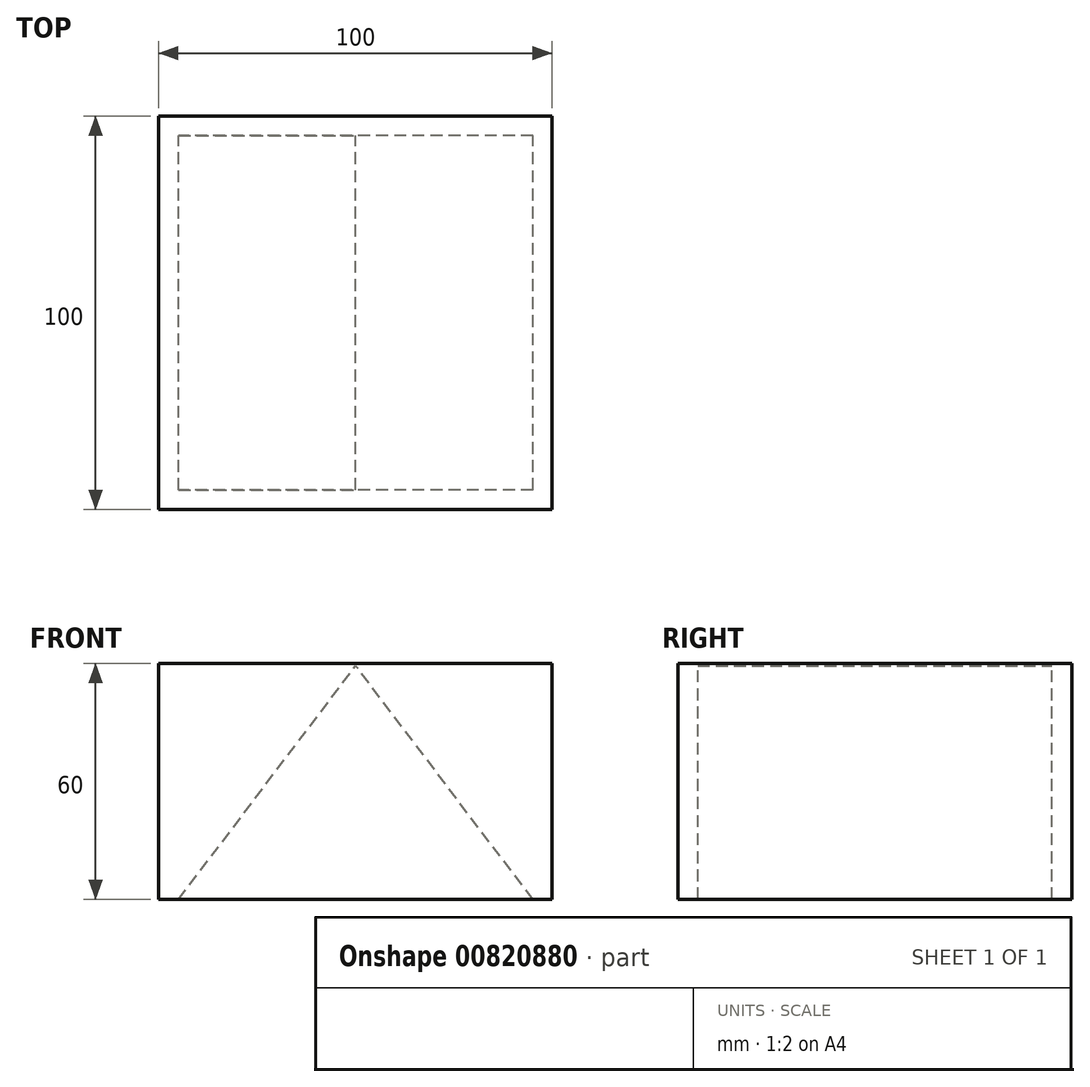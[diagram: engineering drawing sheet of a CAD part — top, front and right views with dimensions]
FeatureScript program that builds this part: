
annotation { "Feature Type Name" : "Feature", "Feature Type Description" : "" }
export const myFeature = defineFeature(function(context is Context, id is Id, definition is map)
    precondition{}
    {
        {
            var Q0;
            Q0=qCreatedBy(makeId("Top.planeOp"),FACE);
            var sketch = newSketch(context, id + "F0", { "sketchPlane" : qUnion([Q0])});
            skLineSegment(sketch, "E0.bottom", {"start": v(0, 0) * mm, "end": v(-100, 0) * mm});
            skLineSegment(sketch, "E0.top", {"start": v(0, 100) * mm, "end": v(-100, 100) * mm});
            skLineSegment(sketch, "E0.left", {"start": v(0, 0) * mm, "end": v(0, 100) * mm});
            skLineSegment(sketch, "E0.right", {"start": v(-100, 0) * mm, "end": v(-100, 100) * mm});
            skSolve(sketch);
        }
        {
            var Q0;
            Q0=makeQuery(id+"F0.imprint","IMPRINT",FACE,{"disambiguationData":[TD([[makeQuery(id+"F0.imprint","IMPRINT",EDGE,{"derivedFrom":sQuery(id+"F0.wireOp",EDGE,"E0.bottom")}),-1.0]])]});
            extrude(context, id + "F1", {"entities" : qUnion([Q0]), "depth" : 60 * mm, "offsetDistance" : 25.4 * mm});
        }
        {
            var Q0;
            Q0=makeQuery(id+"F1.opExtrude","SWEPT_FACE",FACE,{"disambiguationData":[OSD([sQuery(id+"F0.wireOp",EDGE,"E0.top")])]});
            cPlane(context, id + "F2", {"entities" : qUnion([Q0]), "cplaneType" : CPlaneType.OFFSET, "offset" : 5 * mm, "oppositeDirection" : true, "width" : 152.4 * mm, "height" : 152.4 * mm});
        }
        {
            var Q0;
            Q0=makeQuery(id+"F1.opExtrude","SWEPT_FACE",FACE,{"disambiguationData":[OSD([sQuery(id+"F0.wireOp",EDGE,"E0.left")])]});
            cPlane(context, id + "F3", {"entities" : qUnion([Q0]), "cplaneType" : CPlaneType.OFFSET, "offset" : 5 * mm, "oppositeDirection" : true, "width" : 152.4 * mm, "height" : 152.4 * mm});
        }
        {
            var Q0;
            Q0=qCreatedBy(id+"F2.planeOp",FACE);
            var sketch = newSketch(context, id + "F4", { "sketchPlane" : qUnion([Q0])});
            skLineSegment(sketch, "E1", {"start": v(4.9, 0) * mm, "end": v(49.9, 59.36) * mm});
            skLineSegment(sketch, "E2", {"start": v(4.9, 0) * mm, "end": v(4.9, 60) * mm, "construction": true});
            skLineSegment(sketch, "E3", {"start": v(4.9, 60) * mm, "end": v(49.9, 59.36) * mm, "construction": true});
            skLineSegment(sketch, "E4", {"start": v(49.9, 59.36) * mm, "end": v(49.9, 0) * mm, "construction": true});
            skLineSegment(sketch, "E5.MirrorCS", {"start": v(94.9, 0) * mm, "end": v(49.9, 59.36) * mm});
            skLineSegment(sketch, "E6", {"start": v(4.9, 0) * mm, "end": v(94.9, 0) * mm});
            skSolve(sketch);
        }
        {
            var Q0;
            Q0=qSketchRegion(id+"F4",true);
            extrude(context, id + "F5", {"entities" : qUnion([Q0]), "operationType" : NewBodyOperationType.REMOVE, "oppositeDirection" : true, "depth" : 90 * mm, "offsetDistance" : 25.4 * mm});
        }
    });
